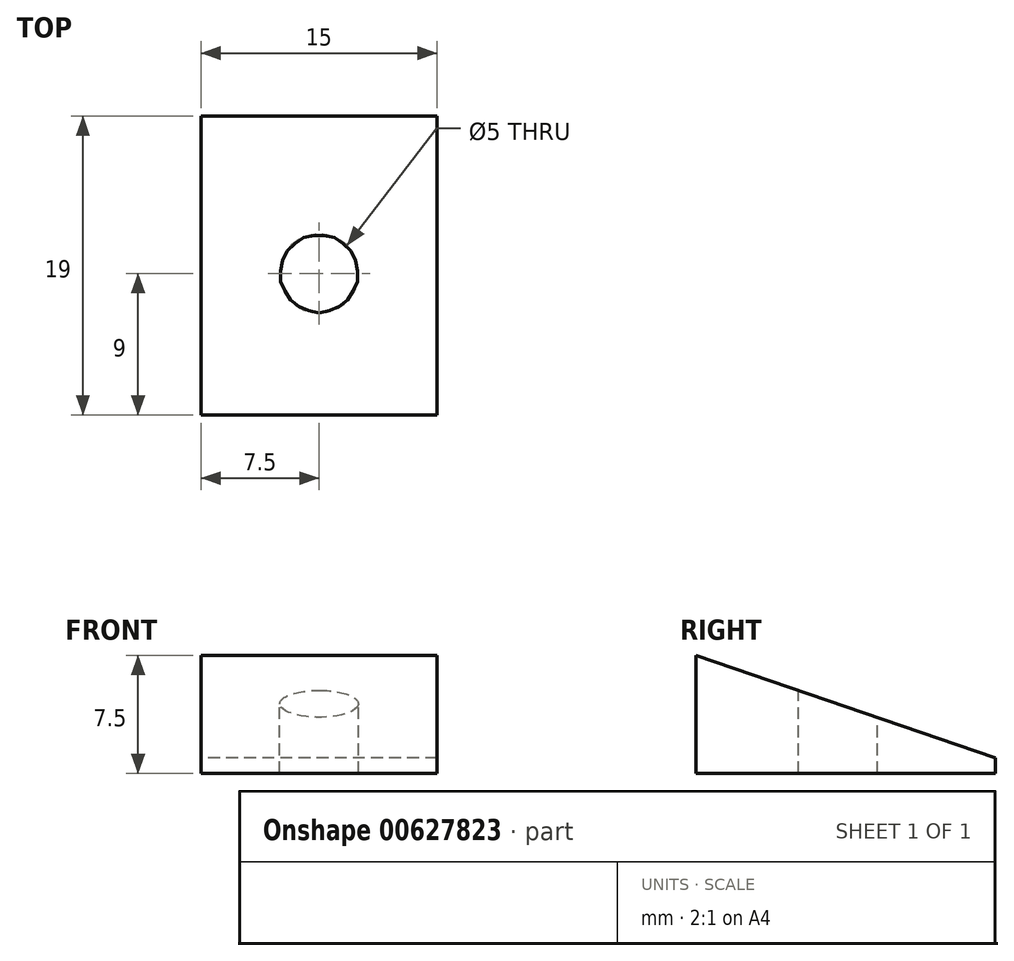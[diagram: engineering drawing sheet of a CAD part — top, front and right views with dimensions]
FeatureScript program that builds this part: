
annotation { "Feature Type Name" : "Feature", "Feature Type Description" : "" }
export const myFeature = defineFeature(function(context is Context, id is Id, definition is map)
    precondition{}
    {
        {
            var Q0;
            Q0=qCreatedBy(makeId("Top.planeOp"),FACE);
            var sketch = newSketch(context, id + "F0", { "sketchPlane" : qUnion([Q0])});
            skCircle(sketch, "E0", {"center": v(0, 0) * mm, "radius": 2.5 * mm});
            skLineSegment(sketch, "E1", {"start": v(-7.5, 0) * mm, "end": v(-7.5, -9) * mm});
            skLineSegment(sketch, "E2", {"start": v(-7.5, -9) * mm, "end": v(7.5, -9) * mm});
            skLineSegment(sketch, "E3", {"start": v(7.5, -9) * mm, "end": v(7.5, 0) * mm});
            skLineSegment(sketch, "E4", {"start": v(7.5, 0) * mm, "end": v(-7.5, 0) * mm});
            skLineSegment(sketch, "E5", {"start": v(-7.5, 0) * mm, "end": v(-7.5, 10) * mm});
            skLineSegment(sketch, "E6", {"start": v(-7.5, 10) * mm, "end": v(7.5, 10) * mm});
            skLineSegment(sketch, "E7", {"start": v(7.5, 10) * mm, "end": v(7.5, 0) * mm});
            skSolve(sketch);
        }
        {
            var Q0;
            Q0=qCreatedBy(makeId("Right.planeOp"),FACE);
            var sketch = newSketch(context, id + "F1", { "sketchPlane" : qUnion([Q0])});
            skLineSegment(sketch, "E8", {"start": v(0, 0) * mm, "end": v(-9, 0) * mm});
            skLineSegment(sketch, "E9", {"start": v(-9, 0) * mm, "end": v(-9, 7.5) * mm});
            skLineSegment(sketch, "E10", {"start": v(-9, 7.5) * mm, "end": v(10, 1) * mm});
            skLineSegment(sketch, "E11", {"start": v(10, 1) * mm, "end": v(10, 0) * mm});
            skLineSegment(sketch, "E12", {"start": v(0, 0) * mm, "end": v(10, 0) * mm});
            skSolve(sketch);
        }
        {
            var Q0;
            Q0=makeQuery(id+"F1.imprint","IMPRINT",FACE,{"disambiguationData":[TD([[makeQuery(id+"F1.imprint","IMPRINT",EDGE,{"derivedFrom":sQuery(id+"F1.wireOp",EDGE,"E8")}),-1.0]])]});
            extrude(context, id + "F2", {"entities" : qUnion([Q0]), "endBound" : BoundingType.SYMMETRIC, "depth" : 15 * mm, "offsetDistance" : 25 * mm});
        }
        {
            var Q0;
            {var subQ0=sQuery(id+"F0.wireOp",EDGE,"E4");var subQ1=sQuery(id+"F0.wireOp",EDGE,"E0");var subQ2=makeQuery(id+"F0.imprint","INTERSECT",VERTEX,{"disambiguationData":[OD(0.0)],"derivedFrom":[subQ1,subQ0]});Q0=makeQuery(id+"F0.imprint","IMPRINT",FACE,{"disambiguationData":[TD([[makeQuery(id+"F0.imprint","IMPRINT",EDGE,{"disambiguationData":[TD([[subQ2,1.0]])],"derivedFrom":subQ1}),1.0]])]});}
            var Q1;
            {var subQ0=sQuery(id+"F0.wireOp",EDGE,"E4");var subQ1=sQuery(id+"F0.wireOp",EDGE,"E0");var subQ2=makeQuery(id+"F0.imprint","INTERSECT",VERTEX,{"disambiguationData":[OD(0.0)],"derivedFrom":[subQ1,subQ0]});Q1=makeQuery(id+"F0.imprint","IMPRINT",FACE,{"disambiguationData":[TD([[makeQuery(id+"F0.imprint","IMPRINT",EDGE,{"disambiguationData":[TD([[subQ2,-1.0]])],"derivedFrom":subQ1}),1.0]])]});}
            extrude(context, id + "F3", {"entities" : qUnion([Q0, Q1]), "operationType" : NewBodyOperationType.REMOVE, "endBound" : BoundingType.SYMMETRIC, "oppositeDirection" : true, "depth" : 20 * mm, "offsetDistance" : 25 * mm});
        }
    });
